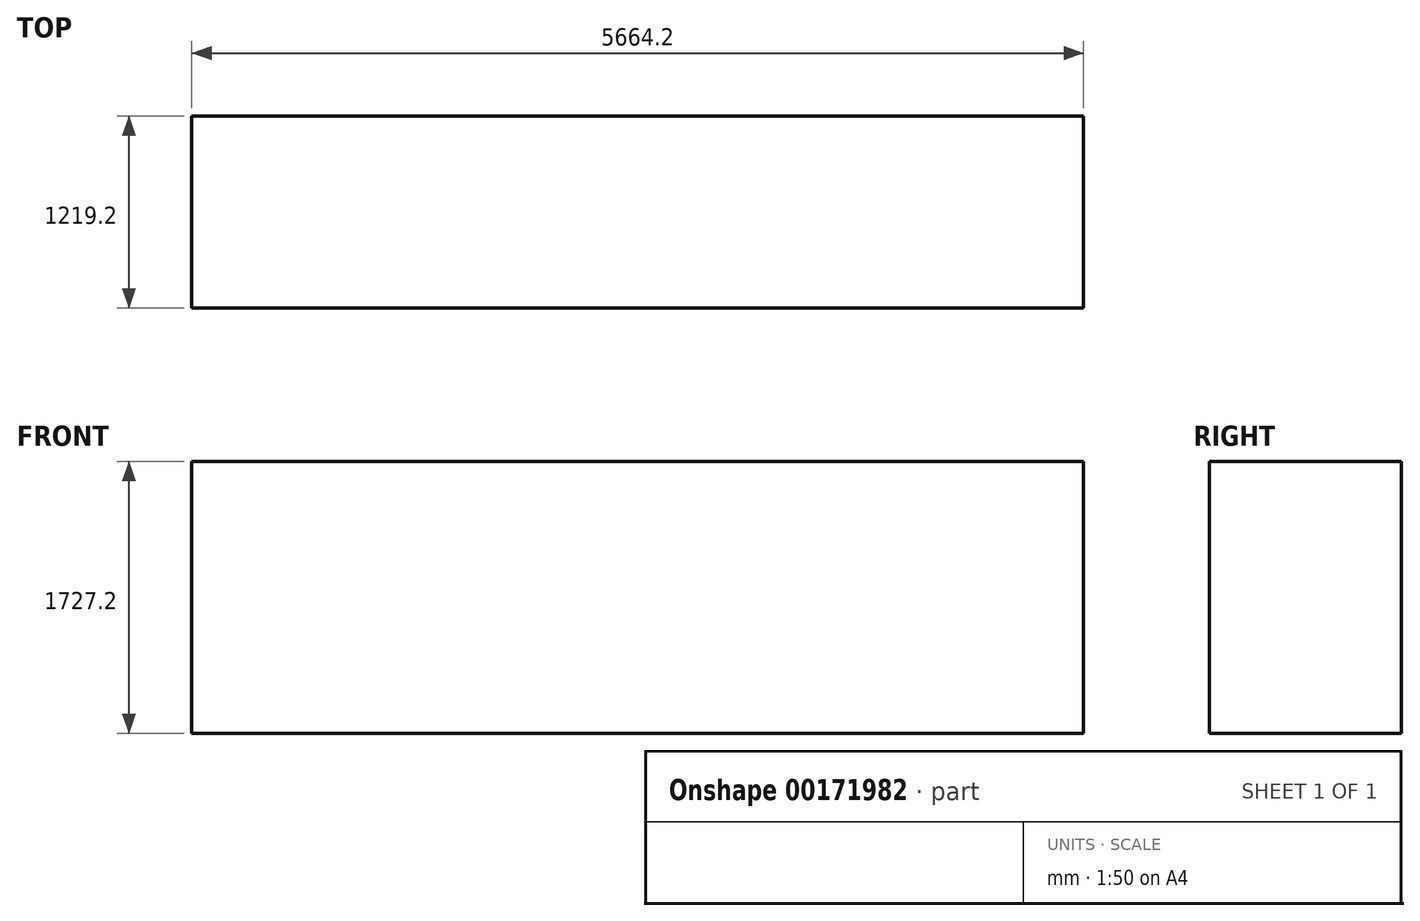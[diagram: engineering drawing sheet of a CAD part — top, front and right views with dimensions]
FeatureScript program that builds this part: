
annotation { "Feature Type Name" : "Feature", "Feature Type Description" : "" }
export const myFeature = defineFeature(function(context is Context, id is Id, definition is map)
    precondition{}
    {
        {
            var Q0;
            Q0=qCreatedBy(makeId("Top.planeOp"),FACE);
            var sketch = newSketch(context, id + "F0", { "sketchPlane" : qUnion([Q0])});
            skLineSegment(sketch, "E0.bottom", {"start": v(-2832.1, 609.6) * mm, "end": v(2832.1, 609.6) * mm});
            skLineSegment(sketch, "E0.top", {"start": v(-2832.1, -609.6) * mm, "end": v(2832.1, -609.6) * mm});
            skLineSegment(sketch, "E0.left", {"start": v(-2832.1, 609.6) * mm, "end": v(-2832.1, -609.6) * mm});
            skLineSegment(sketch, "E0.right", {"start": v(2832.1, 609.6) * mm, "end": v(2832.1, -609.6) * mm});
            skPoint(sketch, "E0.middle", {"position": v(0, 0) * mm});
            skSolve(sketch);
        }
        {
            var Q0;
            Q0 = qSketchRegion(id + "F0", true);
            extrude(context, id + "F1", {"entities" : qUnion([Q0]), "depth" : 1727.2 * mm});
        }
    });
